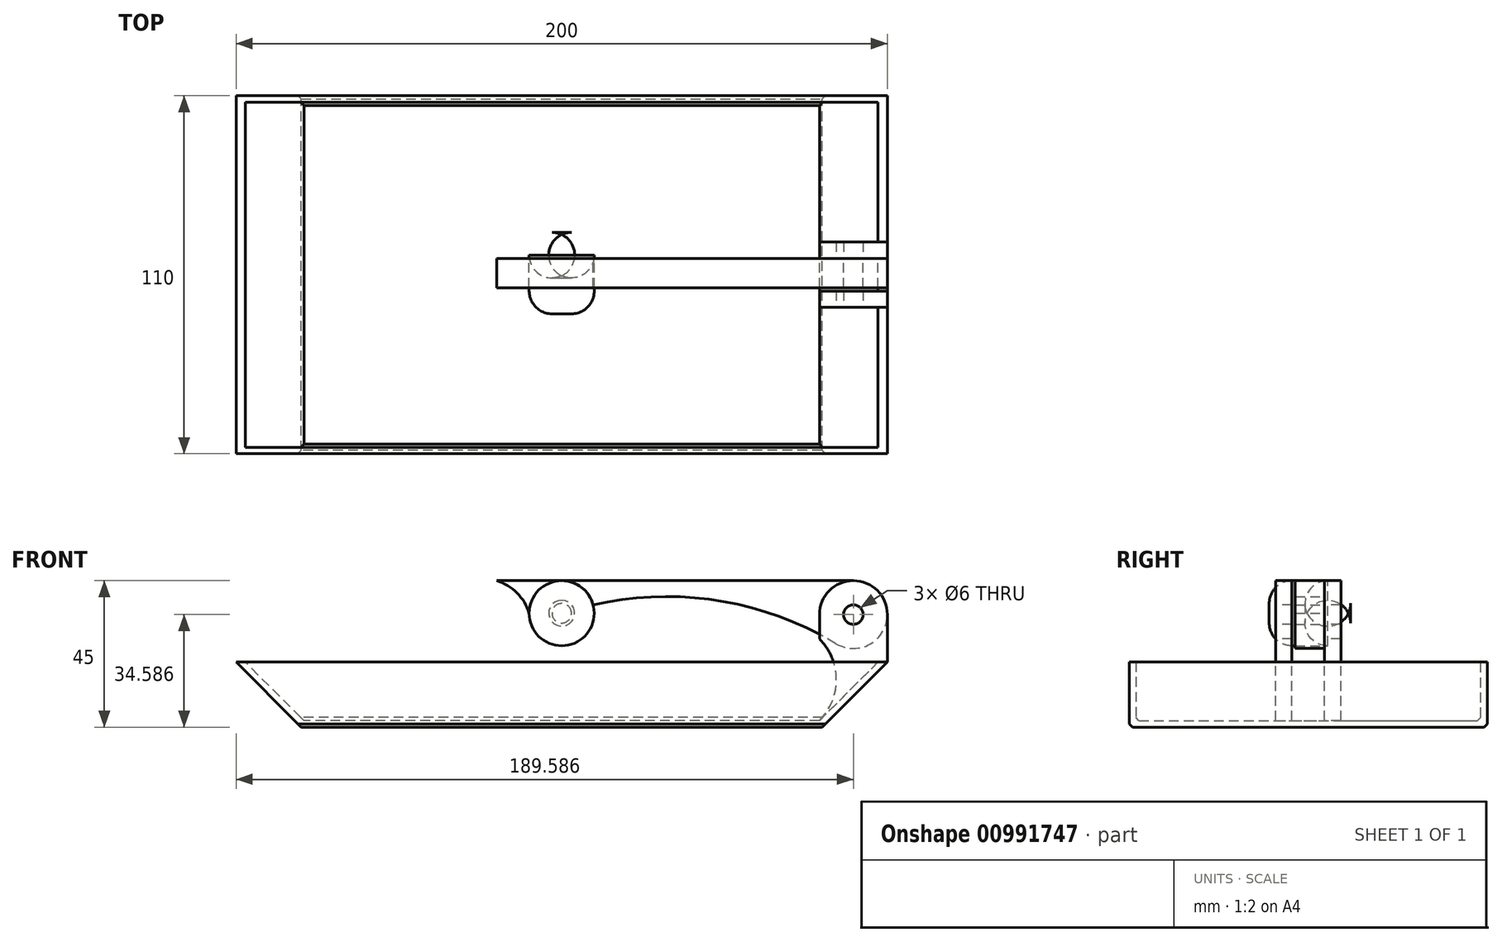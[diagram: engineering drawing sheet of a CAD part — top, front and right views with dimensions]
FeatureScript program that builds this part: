
annotation { "Feature Type Name" : "Feature", "Feature Type Description" : "" }
export const myFeature = defineFeature(function(context is Context, id is Id, definition is map)
    precondition{}
    {
        {
            var Q0;
            Q0=qCreatedBy(makeId("Front.planeOp"),FACE);
            var sketch = newSketch(context, id + "F0", { "sketchPlane" : qUnion([Q0])});
            skLineSegment(sketch, "E0.top", {"start": v(-80, 0) * mm, "end": v(80, 0) * mm});
            skLineSegment(sketch, "E1", {"start": v(-80, 0) * mm, "end": v(-100, 20) * mm});
            skLineSegment(sketch, "E2", {"start": v(100, 20) * mm, "end": v(80, 0) * mm});
            skLineSegment(sketch, "E3", {"start": v(-100, 20) * mm, "end": v(100, 20) * mm});
            skSolve(sketch);
        }
        {
            var Q0;
            Q0 = qSketchRegion(id + "F0", true);
            extrude(context, id + "F1", {"entities" : qUnion([Q0]), "endBound" : BoundingType.SYMMETRIC, "depth" : 110 * mm, "offsetDistance" : 25 * mm});
        }
        {
            var Q0;
            Q0=makeQuery(id+"F1.opExtrude","SWEPT_FACE",FACE,{"disambiguationData":[OSD([sQuery(id+"F0.wireOp",EDGE,"E3")])]});
            shell(context, id + "F2", {"entities" : qUnion([Q0]), "thickness" : 2 * mm});
        }
        {
            var Q0;
            Q0=makeQuery(id+"F1.opExtrude","SWEPT_FACE",FACE,{"disambiguationData":[OSD([sQuery(id+"F0.wireOp",EDGE,"E3")])]});
            var sketch = newSketch(context, id + "F3", { "sketchPlane" : qUnion([Q0])});
            skLineSegment(sketch, "E4", {"start": v(0, 0) * mm, "end": v(139.28, 0) * mm, "construction": true});
            skLineSegment(sketch, "E5.bottom", {"start": v(79.17, 10) * mm, "end": v(100, 10) * mm});
            skLineSegment(sketch, "E5.top", {"start": v(79.17, 5) * mm, "end": v(100, 5) * mm});
            skLineSegment(sketch, "E5.left", {"start": v(79.17, 10) * mm, "end": v(79.17, 5) * mm});
            skLineSegment(sketch, "E5.right", {"start": v(100, 10) * mm, "end": v(100, 5) * mm});
            skLineSegment(sketch, "E6.MirrorCS", {"start": v(79.17, -5) * mm, "end": v(100, -5) * mm});
            skLineSegment(sketch, "E7.MirrorCS", {"start": v(100, -10) * mm, "end": v(100, -5) * mm});
            skLineSegment(sketch, "E8.MirrorCS", {"start": v(79.17, -10) * mm, "end": v(100, -10) * mm});
            skLineSegment(sketch, "E9.MirrorCS", {"start": v(79.17, -10) * mm, "end": v(79.17, -5) * mm});
            skSolve(sketch);
        }
        {
            var Q0;
            Q0 = qSketchRegion(id + "F3", true);
            var Q1;
            Q1=makeQuery(id+"F2.opShell","OFFSET_FACE",FACE,{"disambiguationData":[OSD([sQuery(id+"F0.wireOp",EDGE,"E2")])]});
            extrude(context, id + "F4", {"entities" : qUnion([Q0]), "operationType" : NewBodyOperationType.ADD, "endBound" : BoundingType.UP_TO_SURFACE, "oppositeDirection" : true, "depth" : 25 * mm, "endBoundEntityFace" : qUnion([Q1]), "offsetDistance" : 25 * mm});
        }
        {
            var Q0;
            {var subQ0=sQuery(id+"F3.wireOp",EDGE,"E9.MirrorCS");Q0=makeQuery(id+"F3.imprint","IMPRINT",FACE,{"disambiguationData":[TD([[makeQuery(id+"F3.imprint","IMPRINT",EDGE,{"derivedFrom":subQ0}),-1.0]])]});}
            var Q1;
            {var subQ0=sQuery(id+"F3.wireOp",EDGE,"E7.MirrorCS");Q1=makeQuery(id+"F3.imprint","IMPRINT",FACE,{"disambiguationData":[TD([[makeQuery(id+"F3.imprint","IMPRINT",EDGE,{"derivedFrom":subQ0}),1.0]])]});}
            var Q2;
            {var subQ0=sQuery(id+"F3.wireOp",EDGE,"E5.left");Q2=makeQuery(id+"F3.imprint","IMPRINT",FACE,{"disambiguationData":[TD([[makeQuery(id+"F3.imprint","IMPRINT",EDGE,{"derivedFrom":subQ0}),1.0]])]});}
            var Q3;
            {var subQ0=sQuery(id+"F3.wireOp",EDGE,"E5.right");Q3=makeQuery(id+"F3.imprint","IMPRINT",FACE,{"disambiguationData":[TD([[makeQuery(id+"F3.imprint","IMPRINT",EDGE,{"derivedFrom":subQ0}),1.0]])]});}
            extrude(context, id + "F5", {"entities" : qUnion([Q0, Q1, Q2, Q3]), "operationType" : NewBodyOperationType.ADD, "depth" : 25 * mm, "offsetDistance" : 25 * mm});
        }
        {
            var Q0;
            {var subQ0=sQuery(id+"F3.wireOp",EDGE,"E8.MirrorCS");Q0=makeQuery(id+"F5.boolean.opBoolean","MERGE",FACE,{"derivedFrom":[makeQuery(id+"F4.opExtrude","SWEPT_FACE",FACE,{"disambiguationData":[OSD([subQ0])]}),makeQuery(id+"F5.opExtrude","SWEPT_FACE",FACE,{"disambiguationData":[OSD([subQ0])]})]});}
            var sketch = newSketch(context, id + "F6", { "sketchPlane" : qUnion([Q0])});
            skArc(sketch, "E10", {"start": v(100, 34.59) * mm, "mid": v(89.59, 45) * mm, "end": v(79.17, 34.59) * mm});
            skCircle(sketch, "E11", {"center": v(89.59, 34.59) * mm, "radius": 3 * mm});
            skLineSegment(sketch, "E12", {"start": v(79.17, 34.59) * mm, "end": v(79.17, 45) * mm});
            skLineSegment(sketch, "E13", {"start": v(79.17, 45) * mm, "end": v(100, 45) * mm});
            skLineSegment(sketch, "E14", {"start": v(100, 45) * mm, "end": v(100, 34.59) * mm});
            skArc(sketch, "E15", {"start": v(79.17, 2) * mm, "mid": v(84.37, 14.54) * mm, "end": v(79.17, 27.09) * mm});
            skLineSegment(sketch, "E16", {"start": v(79.17, 27.09) * mm, "end": v(79.17, 2) * mm});
            skSolve(sketch);
        }
        {
            var Q0;
            Q0 = qSketchRegion(id + "F6", true);
            var Q1;
            {var subQ0=sQuery(id+"F3.wireOp",EDGE,"E5.bottom");Q1=makeQuery(id+"F5.boolean.opBoolean","MERGE",FACE,{"derivedFrom":[makeQuery(id+"F4.opExtrude","SWEPT_FACE",FACE,{"disambiguationData":[OSD([subQ0])]}),makeQuery(id+"F5.opExtrude","SWEPT_FACE",FACE,{"disambiguationData":[OSD([subQ0])]})]});}
            extrude(context, id + "F7", {"entities" : qUnion([Q0]), "operationType" : NewBodyOperationType.REMOVE, "endBound" : BoundingType.UP_TO_SURFACE, "oppositeDirection" : true, "depth" : 25 * mm, "endBoundEntityFace" : qUnion([Q1]), "offsetDistance" : 25 * mm});
        }
        {
            var Q0;
            {var subQ0=sQuery(id+"F3.wireOp",EDGE,"E5.top");Q0=makeQuery(id+"F5.boolean.opBoolean","MERGE",FACE,{"derivedFrom":[makeQuery(id+"F4.opExtrude","SWEPT_FACE",FACE,{"disambiguationData":[OSD([subQ0])]}),makeQuery(id+"F5.opExtrude","SWEPT_FACE",FACE,{"disambiguationData":[OSD([subQ0])]})]});}
            var sketch = newSketch(context, id + "F8", { "sketchPlane" : qUnion([Q0])});
            skCircle(sketch, "E17", {"center": v(89.59, 34.59) * mm, "radius": 10.41 * mm});
            skLineSegment(sketch, "E18", {"start": v(89.59, 45) * mm, "end": v(0, 45) * mm});
            skArc(sketch, "E19", {"start": v(0, 45) * mm, "mid": v(-6.12, 27.1) * mm, "end": v(9.68, 37.5) * mm});
            skPoint(sketch, "E20.orphan", {"position": v(0, -90.07) * mm});
            skArc(sketch, "E21", {"start": v(84.2, 25.68) * mm, "mid": v(48.1, 38.88) * mm, "end": v(9.68, 37.5) * mm});
            skCircle(sketch, "E22", {"center": v(89.59, 34.59) * mm, "radius": 3 * mm});
            skLineSegment(sketch, "E23", {"start": v(0, 45) * mm, "end": v(-20, 45) * mm});
            skArc(sketch, "E24", {"start": v(-10, 35) * mm, "mid": v(-13.75, 41.25) * mm, "end": v(-20, 45) * mm});
            skSolve(sketch);
        }
        {
            var Q0;
            Q0 = qSketchRegion(id + "F8", true);
            extrude(context, id + "F9", {"entities" : qUnion([Q0]), "depth" : 9 * mm, "offsetDistance" : 25 * mm});
        }
        {
            var Q0;
            Q0=qCreatedBy(makeId("Front.planeOp"),FACE);
            var sketch = newSketch(context, id + "F10", { "sketchPlane" : qUnion([Q0])});
            skCircle(sketch, "E25", {"center": v(0, 35) * mm, "radius": 10 * mm});
            skSolve(sketch);
        }
        {
            var Q0;
            Q0 = qSketchRegion(id + "F10", true);
            extrude(context, id + "F11", {"entities" : qUnion([Q0]), "operationType" : NewBodyOperationType.ADD, "depth" : 12 * mm, "offsetDistance" : 25 * mm, "hasSecondDirection" : true, "secondDirectionOppositeDirection" : true, "secondDirectionDepth" : 13 * mm});
        }
        {
            var Q0;
            Q0=makeQuery(id+"F11.opExtrude","CAP_FACE",FACE,{"disambiguationData":[OSD([sQuery(id+"F10.wireOp",EDGE,"E25")])],"isStart":false});
            var Q1;
            Q1=makeQuery(id+"F11.opExtrude","CAP_EDGE",EDGE,{"disambiguationData":[OSD([sQuery(id+"F10.wireOp",EDGE,"E25")])],"isStart":true});
            fillet(context, id + "F12", {"entities" : qUnion([Q0, Q1]), "radius" : 7 * mm, "tangentPropagation" : true, "allowEdgeOverflow" : false});
        }
        {
            var Q0;
            {var subQ0=sQuery(id+"F0.wireOp",EDGE,"E0.top");Q0=makeQuery(id+"F2.opShell","OFFSET_EDGE",EDGE,{"disambiguationData":[OSD([subQ0]),TDD([makeQuery(id+"F1.opExtrude","CAP_EDGE",EDGE,{"disambiguationData":[OSD([subQ0])],"isStart":true})])]});}
            var Q1;
            {var subQ0=sQuery(id+"F0.wireOp",EDGE,"E0.top");Q1=makeQuery(id+"F2.opShell","OFFSET_EDGE",EDGE,{"disambiguationData":[OSD([subQ0]),TDD([makeQuery(id+"F1.opExtrude","CAP_EDGE",EDGE,{"disambiguationData":[OSD([subQ0])],"isStart":false})])]});}
            var Q2;
            Q2=makeQuery(id+"F1.opExtrude","CAP_EDGE",EDGE,{"disambiguationData":[OSD([sQuery(id+"F0.wireOp",EDGE,"E0.top")])],"isStart":false});
            var Q3;
            Q3=makeQuery(id+"F1.opExtrude","CAP_EDGE",EDGE,{"disambiguationData":[OSD([sQuery(id+"F0.wireOp",EDGE,"E0.top")])],"isStart":true});
            chamfer(context, id + "F13", {"entities" : qUnion([Q0, Q1, Q2, Q3]), "width" : 1 * mm, "tangentPropagation" : true});
        }
    });
